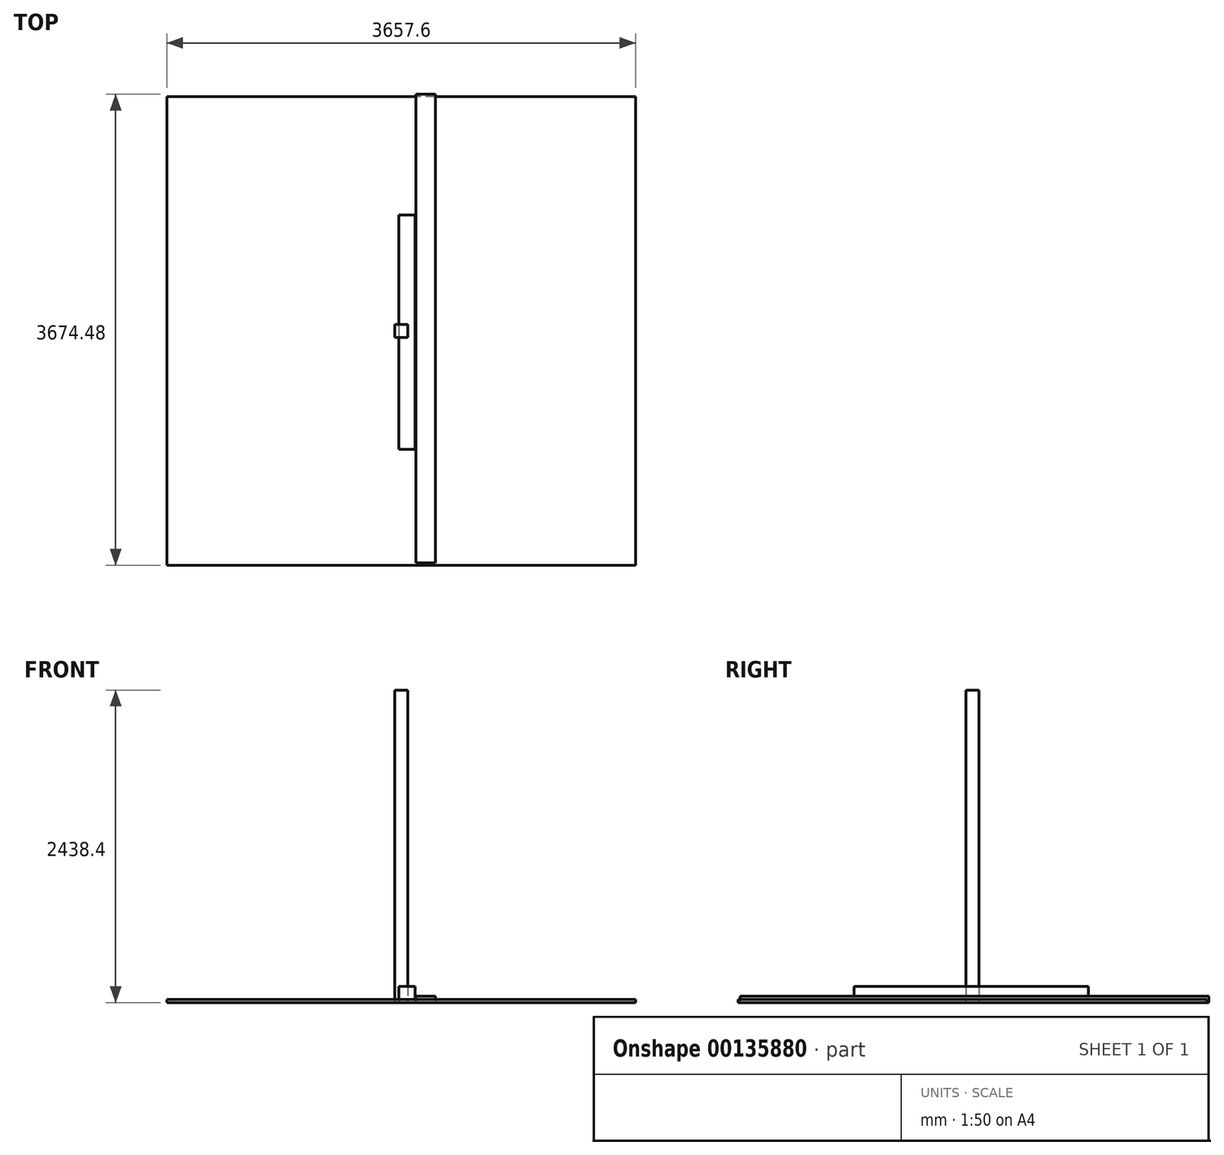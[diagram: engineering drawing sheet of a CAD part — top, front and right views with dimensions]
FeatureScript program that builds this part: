
annotation { "Feature Type Name" : "Feature", "Feature Type Description" : "" }
export const myFeature = defineFeature(function(context is Context, id is Id, definition is map)
    precondition{}
    {
        {
            var Q0;
            Q0=qCreatedBy(makeId("Top.planeOp"),FACE);
            var sketch = newSketch(context, id + "F0", { "sketchPlane" : qUnion([Q0])});
            skLineSegment(sketch, "E0.bottom", {"start": v(-18.17, 904.05) * mm, "end": v(108.83, 904.05) * mm});
            skLineSegment(sketch, "E0.top", {"start": v(-18.17, -924.75) * mm, "end": v(108.83, -924.75) * mm});
            skLineSegment(sketch, "E0.left", {"start": v(-18.17, 904.05) * mm, "end": v(-18.17, -924.75) * mm});
            skLineSegment(sketch, "E0.right", {"start": v(108.83, 904.05) * mm, "end": v(108.83, -924.75) * mm});
            skSolve(sketch);
        }
        {
            var Q0;
            Q0 = qSketchRegion(id + "F0", true);
            extrude(context, id + "F1", {"entities" : qUnion([Q0]), "depth" : 127 * mm, "offsetDistance" : 25.4 * mm});
        }
        {
            var Q0;
            Q0=qCreatedBy(makeId("Top.planeOp"),FACE);
            var sketch = newSketch(context, id + "F2", { "sketchPlane" : qUnion([Q0])});
            skLineSegment(sketch, "E1.bottom", {"start": v(113.88, 1845.68) * mm, "end": v(266.28, 1845.68) * mm});
            skLineSegment(sketch, "E1.top", {"start": v(113.88, -1811.92) * mm, "end": v(266.28, -1811.92) * mm});
            skLineSegment(sketch, "E1.left", {"start": v(113.88, 1845.68) * mm, "end": v(113.88, -1811.92) * mm});
            skLineSegment(sketch, "E1.right", {"start": v(266.28, 1845.68) * mm, "end": v(266.28, -1811.92) * mm});
            skSolve(sketch);
        }
        {
            var Q0;
            Q0 = qSketchRegion(id + "F2", true);
            extrude(context, id + "F3", {"entities" : qUnion([Q0]), "depth" : 50.8 * mm, "offsetDistance" : 25.4 * mm});
        }
        {
            var Q0;
            Q0=qCreatedBy(makeId("Top.planeOp"),FACE);
            var sketch = newSketch(context, id + "F4", { "sketchPlane" : qUnion([Q0])});
            skLineSegment(sketch, "E2.bottom", {"start": v(1828.8, -1828.8) * mm, "end": v(-1828.8, -1828.8) * mm});
            skLineSegment(sketch, "E2.top", {"start": v(1828.8, 1828.8) * mm, "end": v(-1828.8, 1828.8) * mm});
            skLineSegment(sketch, "E2.left", {"start": v(1828.8, -1828.8) * mm, "end": v(1828.8, 1828.8) * mm});
            skLineSegment(sketch, "E2.right", {"start": v(-1828.8, -1828.8) * mm, "end": v(-1828.8, 1828.8) * mm});
            skPoint(sketch, "E2.middle", {"position": v(0, 0) * mm});
            skSolve(sketch);
        }
        {
            var Q0;
            Q0 = qSketchRegion(id + "F4", true);
            extrude(context, id + "F5", {"entities" : qUnion([Q0]), "depth" : 25.4 * mm, "offsetDistance" : 25.4 * mm});
        }
        {
            var Q0;
            Q0=qCreatedBy(makeId("Top.planeOp"),FACE);
            var sketch = newSketch(context, id + "F6", { "sketchPlane" : qUnion([Q0])});
            skLineSegment(sketch, "E3.bottom", {"start": v(50.8, -50.8) * mm, "end": v(-50.8, -50.8) * mm});
            skLineSegment(sketch, "E3.top", {"start": v(50.8, 50.8) * mm, "end": v(-50.8, 50.8) * mm});
            skLineSegment(sketch, "E3.left", {"start": v(50.8, -50.8) * mm, "end": v(50.8, 50.8) * mm});
            skLineSegment(sketch, "E3.right", {"start": v(-50.8, -50.8) * mm, "end": v(-50.8, 50.8) * mm});
            skPoint(sketch, "E3.middle", {"position": v(0, 0) * mm});
            skSolve(sketch);
        }
        {
            var Q0;
            Q0 = qSketchRegion(id + "F6", true);
            extrude(context, id + "F7", {"entities" : qUnion([Q0]), "depth" : 2438.4 * mm, "offsetDistance" : 25.4 * mm});
        }
    });
